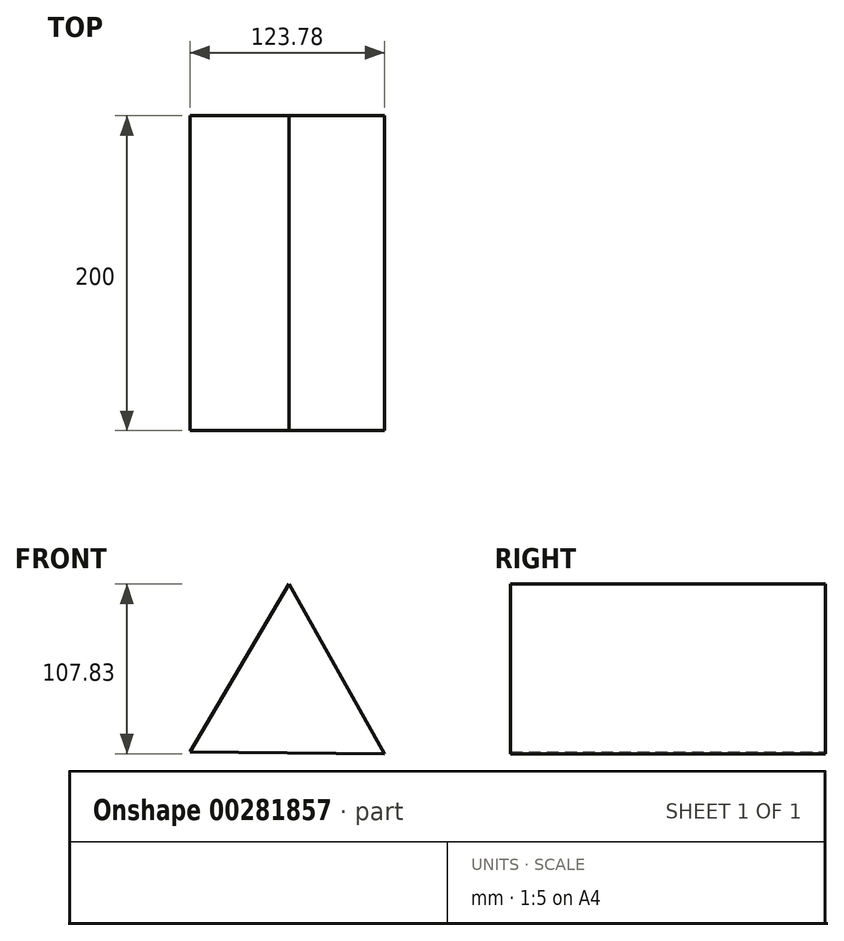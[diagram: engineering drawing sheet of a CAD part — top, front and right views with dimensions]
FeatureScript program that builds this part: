
annotation { "Feature Type Name" : "Feature", "Feature Type Description" : "" }
export const myFeature = defineFeature(function(context is Context, id is Id, definition is map)
    precondition{}
    {
        {
            var Q0;
            Q0=qCreatedBy(makeId("Front.planeOp"),FACE);
            var sketch = newSketch(context, id + "F0", { "sketchPlane" : qUnion([Q0])});
            skCircle(sketch, "E0.cCircle", {"center": v(0, 0) * mm, "radius": 71.47 * mm, "construction": true});
            skLineSegment(sketch, "E0.0", {"start": v(61.52, -36.37) * mm, "end": v(-62.26, -35.1) * mm});
            skLineSegment(sketch, "E0.1", {"start": v(-62.26, -35.1) * mm, "end": v(0.74, 71.46) * mm});
            skLineSegment(sketch, "E0.2", {"start": v(0.74, 71.46) * mm, "end": v(61.52, -36.37) * mm});
            skSolve(sketch);
        }
        {
            var Q0;
            Q0=makeQuery(id+"F0.imprint","IMPRINT",FACE,{"disambiguationData":[TD([[makeQuery(id+"F0.imprint","IMPRINT",EDGE,{"derivedFrom":sQuery(id+"F0.wireOp",EDGE,"E0.0")}),-1.0]])]});
            extrude(context, id + "F1", {"entities" : qUnion([Q0]), "depth" : 200 * mm});
        }
    });
